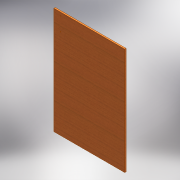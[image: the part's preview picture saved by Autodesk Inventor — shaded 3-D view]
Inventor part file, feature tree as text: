
AUTODESK INVENTOR PART (.ipt)
format: ipt  version: 2016 (Build 200138000, 138)  size: 139,776 bytes
history: native  units: mm
features: extrude x1, sketch x1
ambient origin geometry x8: Origin, YZ Plane, XZ Plane, XY Plane, X Axis, Y Axis, Z Axis, Center Point
bodies: Body1 (feature_tree)
feature tree (2):
  extrude  "Extrusion8"  Depth=10.0mm
  sketch  "Sketch8"  dims[d38=70.0mm d39=20.0mm d42=80.0mm d43=6.0mm d44=50.0mm d45=50.0mm d46=10.0mm d47=0.0mm d48=100.0mm d49=6.0mm]
